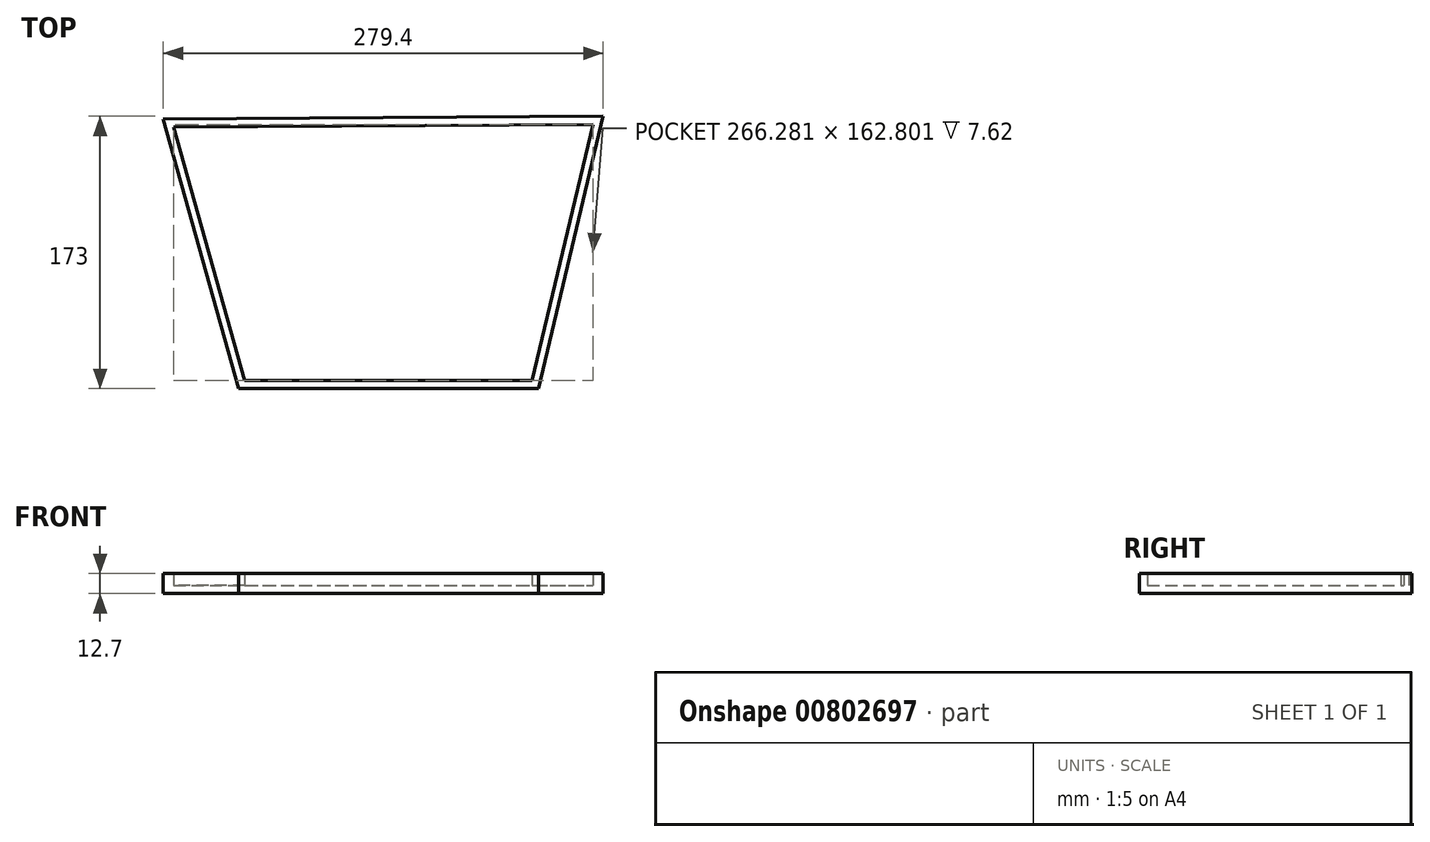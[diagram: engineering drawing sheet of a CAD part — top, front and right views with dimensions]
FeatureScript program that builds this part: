
annotation { "Feature Type Name" : "Feature", "Feature Type Description" : "" }
export const myFeature = defineFeature(function(context is Context, id is Id, definition is map)
    precondition{}
    {
        {
            var Q0;
            Q0=qCreatedBy(makeId("Top.planeOp"),FACE);
            var sketch = newSketch(context, id + "F0", { "sketchPlane" : qUnion([Q0])});
            skLineSegment(sketch, "E0", {"start": v(-79.7, -15.44) * mm, "end": v(110.8, -15.44) * mm});
            skLineSegment(sketch, "E1", {"start": v(110.8, -15.44) * mm, "end": v(151.83, 157.56) * mm});
            skLineSegment(sketch, "E2", {"start": v(-79.7, -15.44) * mm, "end": v(-127.57, 155.8) * mm});
            skLineSegment(sketch, "E3", {"start": v(-127.57, 155.8) * mm, "end": v(151.83, 157.56) * mm});
            skSolve(sketch);
        }
        {
            var Q0;
            Q0 = qSketchRegion(id + "F0", true);
            extrude(context, id + "F1", {"entities" : qUnion([Q0]), "depth" : 12.7 * mm, "offsetDistance" : 25.4 * mm});
        }
        {
            var Q0;
            Q0=makeQuery(id+"F1.opExtrude","CAP_FACE",FACE,{"disambiguationData":[OSD([sQuery(id+"F0.wireOp",EDGE,"E0"),sQuery(id+"F0.wireOp",EDGE,"E1"),sQuery(id+"F0.wireOp",EDGE,"E2"),sQuery(id+"F0.wireOp",EDGE,"E3")])],"isStart":false});
            shell(context, id + "F2", {"entities" : qUnion([Q0]), "thickness" : 5.08 * mm});
        }
    });
